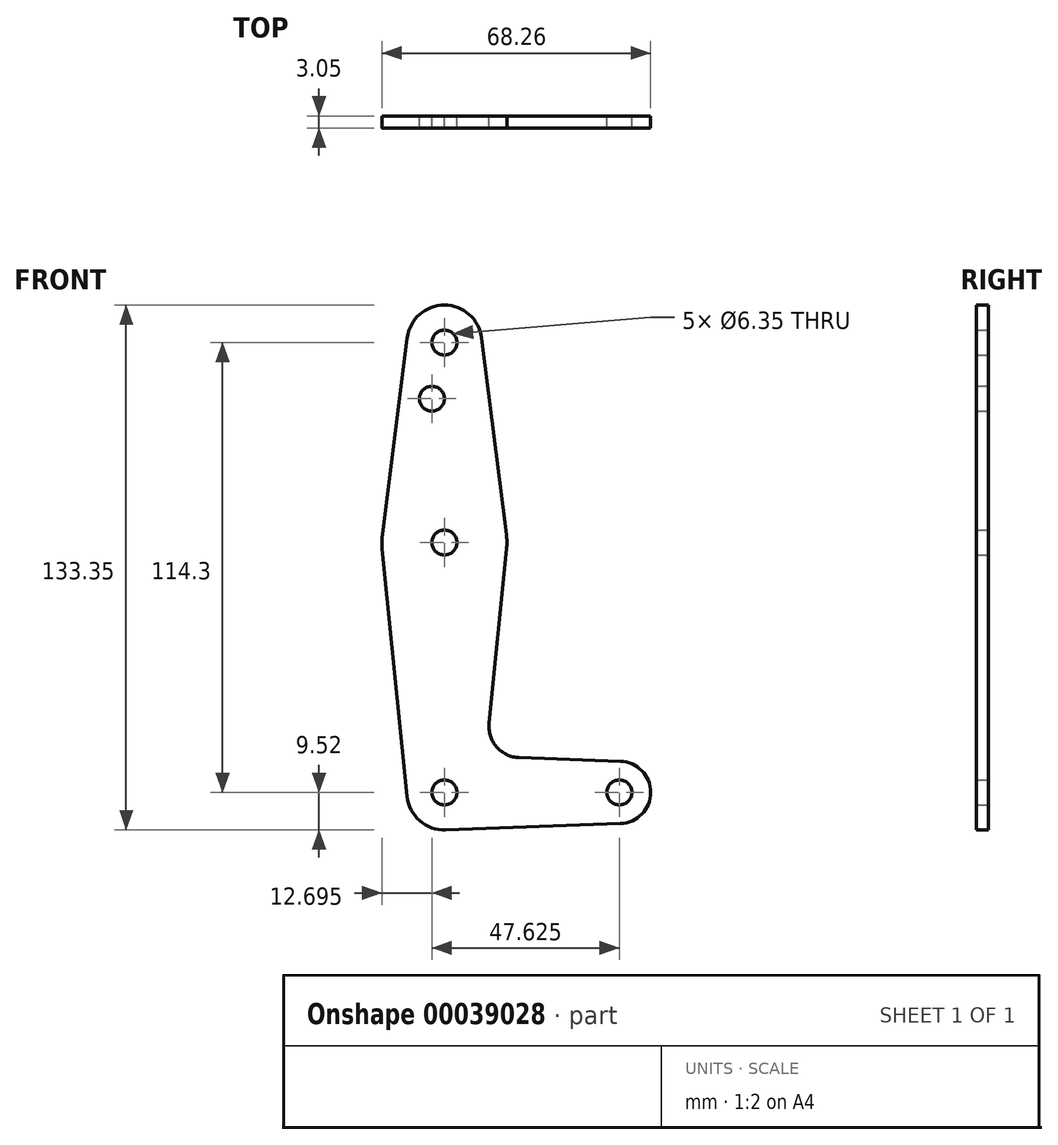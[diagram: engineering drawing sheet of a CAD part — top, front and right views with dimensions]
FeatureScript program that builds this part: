
annotation { "Feature Type Name" : "Feature", "Feature Type Description" : "" }
export const myFeature = defineFeature(function(context is Context, id is Id, definition is map)
    precondition{}
    {
        {
            var Q0;
            Q0=qCreatedBy(makeId("Front.planeOp"),FACE);
            var sketch = newSketch(context, id + "F0", { "sketchPlane" : qUnion([Q0])});
            skCircle(sketch, "E0", {"center": v(0, 0) * mm, "radius": 9.53 * mm});
            skCircle(sketch, "E1", {"center": v(0, 63.5) * mm, "radius": 15.88 * mm});
            skCircle(sketch, "E2", {"center": v(0, 114.3) * mm, "radius": 9.53 * mm});
            skCircle(sketch, "E3", {"center": v(44.45, 0) * mm, "radius": 7.94 * mm});
            skLineSegment(sketch, "E4", {"start": v(0, 114.3) * mm, "end": v(0, 63.5) * mm, "construction": true});
            skLineSegment(sketch, "E5", {"start": v(0, 0) * mm, "end": v(0, 63.5) * mm, "construction": true});
            skLineSegment(sketch, "E6", {"start": v(0, 0) * mm, "end": v(44.45, 0) * mm, "construction": true});
            skLineSegment(sketch, "E7", {"start": v(9.45, 115.5) * mm, "end": v(15.75, 65.48) * mm});
            skLineSegment(sketch, "E8", {"start": v(-9.45, 115.5) * mm, "end": v(-15.75, 65.48) * mm});
            skLineSegment(sketch, "E9", {"start": v(-15.8, 61.91) * mm, "end": v(-9.48, -0.95) * mm});
            skLineSegment(sketch, "E10", {"start": v(15.8, 61.91) * mm, "end": v(11.34, 17.6) * mm});
            skLineSegment(sketch, "E11", {"start": v(18.97, 8.85) * mm, "end": v(44.73, 7.93) * mm});
            skLineSegment(sketch, "E12", {"start": v(44.73, -7.93) * mm, "end": v(0.34, -9.52) * mm});
            skCircle(sketch, "E13", {"center": v(0, 114.3) * mm, "radius": 3.18 * mm});
            skCircle(sketch, "E14", {"center": v(0, 63.5) * mm, "radius": 3.18 * mm});
            skCircle(sketch, "E15", {"center": v(0, 0) * mm, "radius": 3.18 * mm});
            skCircle(sketch, "E16", {"center": v(44.45, 0) * mm, "radius": 3.18 * mm});
            skCircle(sketch, "E17", {"center": v(-3.17, 100.03) * mm, "radius": 3.18 * mm});
            skArc(sketch, "E18.filletArc", {"start": v(11.34, 17.6) * mm, "mid": v(13.26, 11.57) * mm, "end": v(18.97, 8.85) * mm});
            skSolve(sketch);
        }
        {
            var Q0;
            Q0 = qSketchRegion(id + "F0", true);
            extrude(context, id + "F1", {"entities" : qUnion([Q0]), "depth" : 3.05 * mm});
        }
    });
